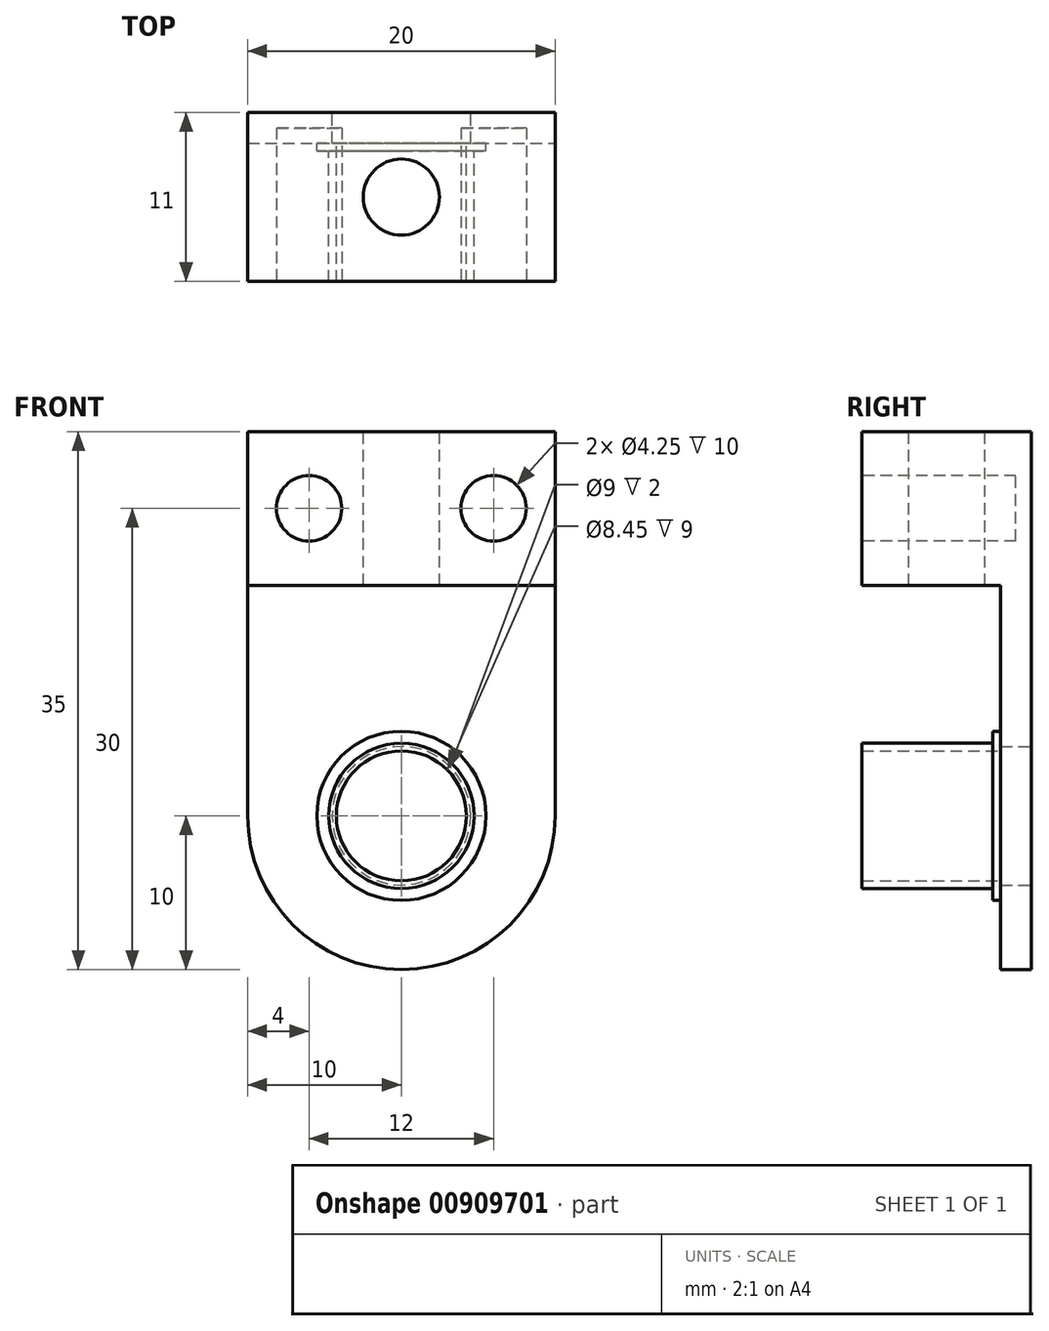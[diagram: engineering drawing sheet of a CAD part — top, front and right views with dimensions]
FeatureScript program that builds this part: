
annotation { "Feature Type Name" : "Feature", "Feature Type Description" : "" }
export const myFeature = defineFeature(function(context is Context, id is Id, definition is map)
    precondition{}
    {
        {
            var Q0;
            Q0=qCreatedBy(makeId("Front.planeOp"),FACE);
            var sketch = newSketch(context, id + "F0", { "sketchPlane" : qUnion([Q0])});
            skPoint(sketch, "E0.middle", {"position": v(0, 0) * mm});
            skCircle(sketch, "E1", {"center": v(0, 0) * mm, "radius": 13 * mm});
            skCircle(sketch, "E2", {"center": v(0, 0) * mm, "radius": 5 * mm});
            skCircle(sketch, "E3", {"center": v(0, 0) * mm, "radius": 10 * mm});
            skLineSegment(sketch, "E4.bottom", {"start": v(-10, 0) * mm, "end": v(10, 0) * mm});
            skLineSegment(sketch, "E4.top", {"start": v(-10, 25) * mm, "end": v(10, 25) * mm});
            skLineSegment(sketch, "E4.left", {"start": v(-10, 0) * mm, "end": v(-10, 25) * mm});
            skLineSegment(sketch, "E4.right", {"start": v(10, 0) * mm, "end": v(10, 25) * mm});
            skCircle(sketch, "E5", {"center": v(0, 0) * mm, "radius": 4.5 * mm});
            skSolve(sketch);
        }
        {
            var Q0;
            {var subQ5=sQuery(id+"F0.wireOp",EDGE,"E4.top");Q0=makeQuery(id+"F0.imprint","IMPRINT",FACE,{"disambiguationData":[TD([[makeQuery(id+"F0.imprint","IMPRINT",EDGE,{"derivedFrom":subQ5}),-1.0]])]});}
            var Q1;
            {var subQ0=sQuery(id+"F0.wireOp",EDGE,"E4.left");var subQ1=sQuery(id+"F0.wireOp",EDGE,"E1");var subQ2=makeQuery(id+"F0.imprint","INTERSECT",VERTEX,{"derivedFrom":[subQ1,subQ0]});Q1=makeQuery(id+"F0.imprint","IMPRINT",FACE,{"disambiguationData":[TD([[makeQuery(id+"F0.imprint","IMPRINT",EDGE,{"disambiguationData":[TD([[subQ2,1.0]])],"derivedFrom":subQ1}),1.0]])]});}
            var Q2;
            {var subQ0=sQuery(id+"F0.wireOp",EDGE,"E4.bottom");var subQ1=sQuery(id+"F0.wireOp",EDGE,"E2");var subQ2=makeQuery(id+"F0.imprint","INTERSECT",VERTEX,{"disambiguationData":[OD(0.0)],"derivedFrom":[subQ1,subQ0]});Q2=makeQuery(id+"F0.imprint","IMPRINT",FACE,{"disambiguationData":[TD([[makeQuery(id+"F0.imprint","IMPRINT",EDGE,{"disambiguationData":[TD([[subQ2,1.0]])],"derivedFrom":subQ1}),-1.0]])]});}
            var Q3;
            {var subQ0=sQuery(id+"F0.wireOp",EDGE,"E4.bottom");var subQ1=sQuery(id+"F0.wireOp",EDGE,"E2");var subQ2=makeQuery(id+"F0.imprint","INTERSECT",VERTEX,{"disambiguationData":[OD(0.0)],"derivedFrom":[subQ1,subQ0]});Q3=makeQuery(id+"F0.imprint","IMPRINT",FACE,{"disambiguationData":[TD([[makeQuery(id+"F0.imprint","IMPRINT",EDGE,{"disambiguationData":[TD([[subQ2,-1.0]])],"derivedFrom":subQ1}),-1.0]])]});}
            var Q4;
            {var subQ0=sQuery(id+"F0.wireOp",EDGE,"E4.bottom");var subQ1=sQuery(id+"F0.wireOp",EDGE,"E2");var subQ2=makeQuery(id+"F0.imprint","INTERSECT",VERTEX,{"disambiguationData":[OD(0.0)],"derivedFrom":[subQ1,subQ0]});Q4=makeQuery(id+"F0.imprint","IMPRINT",FACE,{"disambiguationData":[TD([[makeQuery(id+"F0.imprint","IMPRINT",EDGE,{"disambiguationData":[TD([[subQ2,-1.0]])],"derivedFrom":subQ1}),1.0]])]});}
            var Q5;
            {var subQ0=sQuery(id+"F0.wireOp",EDGE,"E4.bottom");var subQ1=sQuery(id+"F0.wireOp",EDGE,"E2");var subQ2=makeQuery(id+"F0.imprint","INTERSECT",VERTEX,{"disambiguationData":[OD(0.0)],"derivedFrom":[subQ1,subQ0]});Q5=makeQuery(id+"F0.imprint","IMPRINT",FACE,{"disambiguationData":[TD([[makeQuery(id+"F0.imprint","IMPRINT",EDGE,{"disambiguationData":[TD([[subQ2,1.0]])],"derivedFrom":subQ1}),1.0]])]});}
            extrude(context, id + "F1", {"entities" : qUnion([Q0, Q1, Q2, Q3, Q4, Q5]), "depth" : 2 * mm, "offsetDistance" : 25 * mm});
        }
        {
            var Q0;
            Q0=makeQuery(id+"F1.opExtrude","CAP_FACE",FACE,{"disambiguationData":[OSD([sQuery(id+"F0.wireOp",EDGE,"E3"),sQuery(id+"F0.wireOp",EDGE,"E4.top"),sQuery(id+"F0.wireOp",EDGE,"E4.left"),sQuery(id+"F0.wireOp",EDGE,"E4.right"),sQuery(id+"F0.wireOp",EDGE,"E5")])],"isStart":false});
            var sketch = newSketch(context, id + "F2", { "sketchPlane" : qUnion([Q0])});
            skCircle(sketch, "E6", {"center": v(0, 0) * mm, "radius": 4.72 * mm});
            skCircle(sketch, "E7", {"center": v(0, 0) * mm, "radius": 4.22 * mm});
            skSolve(sketch);
        }
        {
            var Q0;
            Q0 = qSketchRegion(id + "F2", true);
            extrude(context, id + "F3", {"entities" : qUnion([Q0]), "operationType" : NewBodyOperationType.ADD, "depth" : 9 * mm, "offsetDistance" : 25 * mm});
        }
        {
            var Q0;
            Q0=makeQuery(id+"F1.opExtrude","CAP_FACE",FACE,{"disambiguationData":[OSD([sQuery(id+"F0.wireOp",EDGE,"E3"),sQuery(id+"F0.wireOp",EDGE,"E4.top"),sQuery(id+"F0.wireOp",EDGE,"E4.left"),sQuery(id+"F0.wireOp",EDGE,"E4.right"),sQuery(id+"F0.wireOp",EDGE,"E5")])],"isStart":false});
            var sketch = newSketch(context, id + "F4", { "sketchPlane" : qUnion([Q0])});
            skLineSegment(sketch, "E8.bottom", {"start": v(-10, 25) * mm, "end": v(10, 25) * mm});
            skLineSegment(sketch, "E8.top", {"start": v(-10, 15) * mm, "end": v(10, 15) * mm});
            skLineSegment(sketch, "E8.left", {"start": v(-10, 25) * mm, "end": v(-10, 15) * mm});
            skLineSegment(sketch, "E8.right", {"start": v(10, 25) * mm, "end": v(10, 15) * mm});
            skSolve(sketch);
        }
        {
            var Q0;
            Q0=makeQuery(id+"F4.imprint","IMPRINT",FACE,{"disambiguationData":[TD([[makeQuery(id+"F4.imprint","IMPRINT",EDGE,{"derivedFrom":sQuery(id+"F4.wireOp",EDGE,"E8.bottom")}),-1.0]])]});
            extrude(context, id + "F5", {"entities" : qUnion([Q0]), "operationType" : NewBodyOperationType.ADD, "depth" : 9 * mm, "offsetDistance" : 25 * mm});
        }
        {
            var Q0;
            Q0=makeQuery(id+"F5.boolean.opBoolean","MERGE",FACE,{"derivedFrom":[makeQuery(id+"F1.opExtrude","SWEPT_FACE",FACE,{"disambiguationData":[OSD([sQuery(id+"F0.wireOp",EDGE,"E4.top")])]}),makeQuery(id+"F5.opExtrude","SWEPT_FACE",FACE,{"disambiguationData":[OSD([sQuery(id+"F4.wireOp",EDGE,"E8.bottom")])]})]});
            var sketch = newSketch(context, id + "F6", { "sketchPlane" : qUnion([Q0])});
            skCircle(sketch, "E9", {"center": v(0, -5.5) * mm, "radius": 2.48 * mm});
            skSolve(sketch);
        }
        {
            var Q0;
            Q0 = qSketchRegion(id + "F6", true);
            extrude(context, id + "F7", {"entities" : qUnion([Q0]), "depth" : -10 * mm, "offsetDistance" : 25 * mm});
        }
        {
            var Q0;
            Q0=makeQuery(id+"F7.opExtrude","SWEPT_BODY",BODY,{"disambiguationData":[OSD([sQuery(id+"F6.wireOp",EDGE,"E9")])]});
            var Q1;
            Q1=makeQuery(id+"F1.opExtrude","SWEPT_BODY",BODY,{"disambiguationData":[OSD([sQuery(id+"F0.wireOp",EDGE,"E3"),sQuery(id+"F0.wireOp",EDGE,"E4.top"),sQuery(id+"F0.wireOp",EDGE,"E4.left"),sQuery(id+"F0.wireOp",EDGE,"E4.right"),sQuery(id+"F0.wireOp",EDGE,"E5")])]});
            booleanBodies(context, id + "F8", {"operationType" : BooleanOperationType.SUBTRACTION, "tools" : qUnion([Q0]), "targets" : qUnion([Q1])});
        }
        {
            var Q0;
            Q0=makeQuery(id+"F5.opExtrude","CAP_FACE",FACE,{"disambiguationData":[OSD([sQuery(id+"F4.wireOp",EDGE,"E8.bottom"),sQuery(id+"F4.wireOp",EDGE,"E8.top"),sQuery(id+"F4.wireOp",EDGE,"E8.left"),sQuery(id+"F4.wireOp",EDGE,"E8.right")])],"isStart":false});
            var sketch = newSketch(context, id + "F9", { "sketchPlane" : qUnion([Q0])});
            skCircle(sketch, "E10", {"center": v(-6, 20) * mm, "radius": 2.12 * mm});
            skCircle(sketch, "E11", {"center": v(6, 20) * mm, "radius": 2.12 * mm});
            skSolve(sketch);
        }
        {
            var Q0;
            Q0 = qSketchRegion(id + "F9", true);
            extrude(context, id + "F10", {"entities" : qUnion([Q0]), "depth" : -10 * mm, "offsetDistance" : 25 * mm});
        }
        {
            var Q0;
            Q0=makeQuery(id+"F10.opExtrude","SWEPT_BODY",BODY,{"disambiguationData":[OSD([sQuery(id+"F9.wireOp",EDGE,"E11")])]});
            var Q1;
            Q1=makeQuery(id+"F10.opExtrude","SWEPT_BODY",BODY,{"disambiguationData":[OSD([sQuery(id+"F9.wireOp",EDGE,"E10")])]});
            var Q2;
            Q2=makeQuery(id+"F1.opExtrude","SWEPT_BODY",BODY,{"disambiguationData":[OSD([sQuery(id+"F0.wireOp",EDGE,"E3"),sQuery(id+"F0.wireOp",EDGE,"E4.top"),sQuery(id+"F0.wireOp",EDGE,"E4.left"),sQuery(id+"F0.wireOp",EDGE,"E4.right"),sQuery(id+"F0.wireOp",EDGE,"E5")])]});
            booleanBodies(context, id + "F11", {"operationType" : BooleanOperationType.SUBTRACTION, "tools" : qUnion([Q0, Q1]), "targets" : qUnion([Q2])});
        }
        {
            var Q0;
            Q0=makeQuery(id+"F1.opExtrude","CAP_FACE",FACE,{"disambiguationData":[OSD([sQuery(id+"F0.wireOp",EDGE,"E3"),sQuery(id+"F0.wireOp",EDGE,"E4.top"),sQuery(id+"F0.wireOp",EDGE,"E4.left"),sQuery(id+"F0.wireOp",EDGE,"E4.right"),sQuery(id+"F0.wireOp",EDGE,"E5")])],"isStart":false});
            var sketch = newSketch(context, id + "F12", { "sketchPlane" : qUnion([Q0])});
            skCircle(sketch, "E12", {"center": v(0, 0) * mm, "radius": 5.5 * mm});
            skCircle(sketch, "E13", {"center": v(0, 0) * mm, "radius": 4.72 * mm});
            skSolve(sketch);
        }
        {
            var Q0;
            Q0 = qSketchRegion(id + "F12", true);
            extrude(context, id + "F13", {"entities" : qUnion([Q0]), "operationType" : NewBodyOperationType.ADD, "depth" : 0.5 * mm, "offsetDistance" : 25 * mm});
        }
    });
